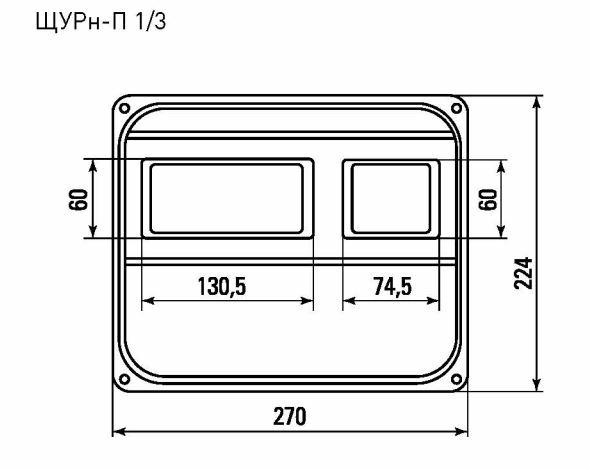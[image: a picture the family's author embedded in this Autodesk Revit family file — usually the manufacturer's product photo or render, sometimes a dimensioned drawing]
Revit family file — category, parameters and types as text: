
# Revit family: EKF_EE_ЩУРн_два_отсека_(БУР)_IP31_PROxima
name_source: partatom
category: Электрооборудование
units: mm (PartAtom-declared; Revit-internal decimal feet)

## family parameters
Всегда вертикально = Да
На основе рабочей плоскости = Нет
Общий = Нет
При загрузке вырезать с полостями = Нет
Размер круглого соединителя = Использовать диаметр
Тип детали = Силовой щит
Точка расчета площади = Да

## types (4) — shared parameters
ADSK_Единица измерения = компл.
ADSK_Завод-изготовитель = EKF
ADSK_Классификация нагрузок = Прочее
ADSK_Количество = 1
ADSK_Количество фаз = 3
ADSK_Коэффициент мощности = 1
ADSK_Материал = RAL 7035_Сталь
ADSK_Напряжение = 400 В
ADSK_Номинальная мощность = 0 Вт
ADSK_Полная мощность = 0 В·А
ADSK_Размер_Ширина = 310 мм
ADSK_Ток = 125 А
Изготовитель = EKF
Количество DIN-реек = 1
Серия номенклатуры = PROxima
Степень защиты IP = IP31
ТВ = EKF
Тип установки = Навесной
zero-valued in all types: Максимальное количество модулей

## per-type parameters (varying)
| type | ADSK_Код изделия | ADSK_Марка | ADSK_Масса | ADSK_Наименование | ADSK_Обозначение | ADSK_Размер_Высота | ADSK_Размер_Глубина | Количество модулей на DIN-рейке | Описание | Тип |
| ЩУРн-1/14 (Э) два отсека (БУР) (450х310х120) IP31 EKF PROxima | mb23-1/14e | ЩУРн-1/14 (Э) два отсека (БУР) IP31 | 4.93 | Щит учетно-распред. навесной ЩУРн-1/14 (Э) два отсека (БУР) (450х310х120) IP31 EKF PROxima | ЩУРн-1/14 (Э) два отсека (БУР) IP31 | 450 мм | 120 мм | 14 | Щит учетно-распред. навесной ЩУРн-1/14 (Э) два отсека (БУР) (450х310х120) IP31 EKF PROxima | 42 мм |
| ЩУРн-1/14 два отсека (БУР) (450х310х140) IP31 EKF PROxima | mb23-1/14i | ЩУРн-1/14 два отсека (БУР) IP31 | 5.1 | Щит учетно-распред. навесной ЩУРн-1/14 два отсека (БУР) (450х310х140) IP31 EKF PROxima | ЩУРн-1/14 два отсека (БУР) IP31 | 450 мм | 140 мм | 14 | Щит учетно-распред. навесной ЩУРн-1/14 два отсека (БУР) (450х310х140) IP31 EKF PROxima | 43 мм |
| ЩУРн-3/15 два отсека (БУР) (520х310х160) IP31 EKF PROxima | mb23-3/15i | ЩУРн-3/15 два отсека (БУР) IP31 | 6.8 | Щит учетно-распред. навесной ЩУРн-3/15 два отсека (БУР) (520х310х160) IP31 EKF PROxima | ЩУРн-3/15 два отсека (БУР) IP31 | 520 мм | 160 мм | 15 | Щит учетно-распред. навесной ЩУРн-3/15 два отсека (БУР) (520х310х160) IP31 EKF PROxima | 44 мм |
| ЩУРн-3/24 два отсека (БУР) (620х310х160) IP31 EKF PROxima | mb23-3/24i | ЩУРн-3/24 два отсека (БУР) IP31 | 7.95 | Щит учетно-распред. навесной ЩУРн-3/24 два отсека (БУР) (620х310х160) IP31 EKF PROxima | ЩУРн-3/24 два отсека (БУР) IP31 | 620 мм | 160 мм | 27 | Щит учетно-распред. навесной ЩУРн-3/24 два отсека (БУР) (620х310х160) IP31 EKF PROxima | 45 мм |
